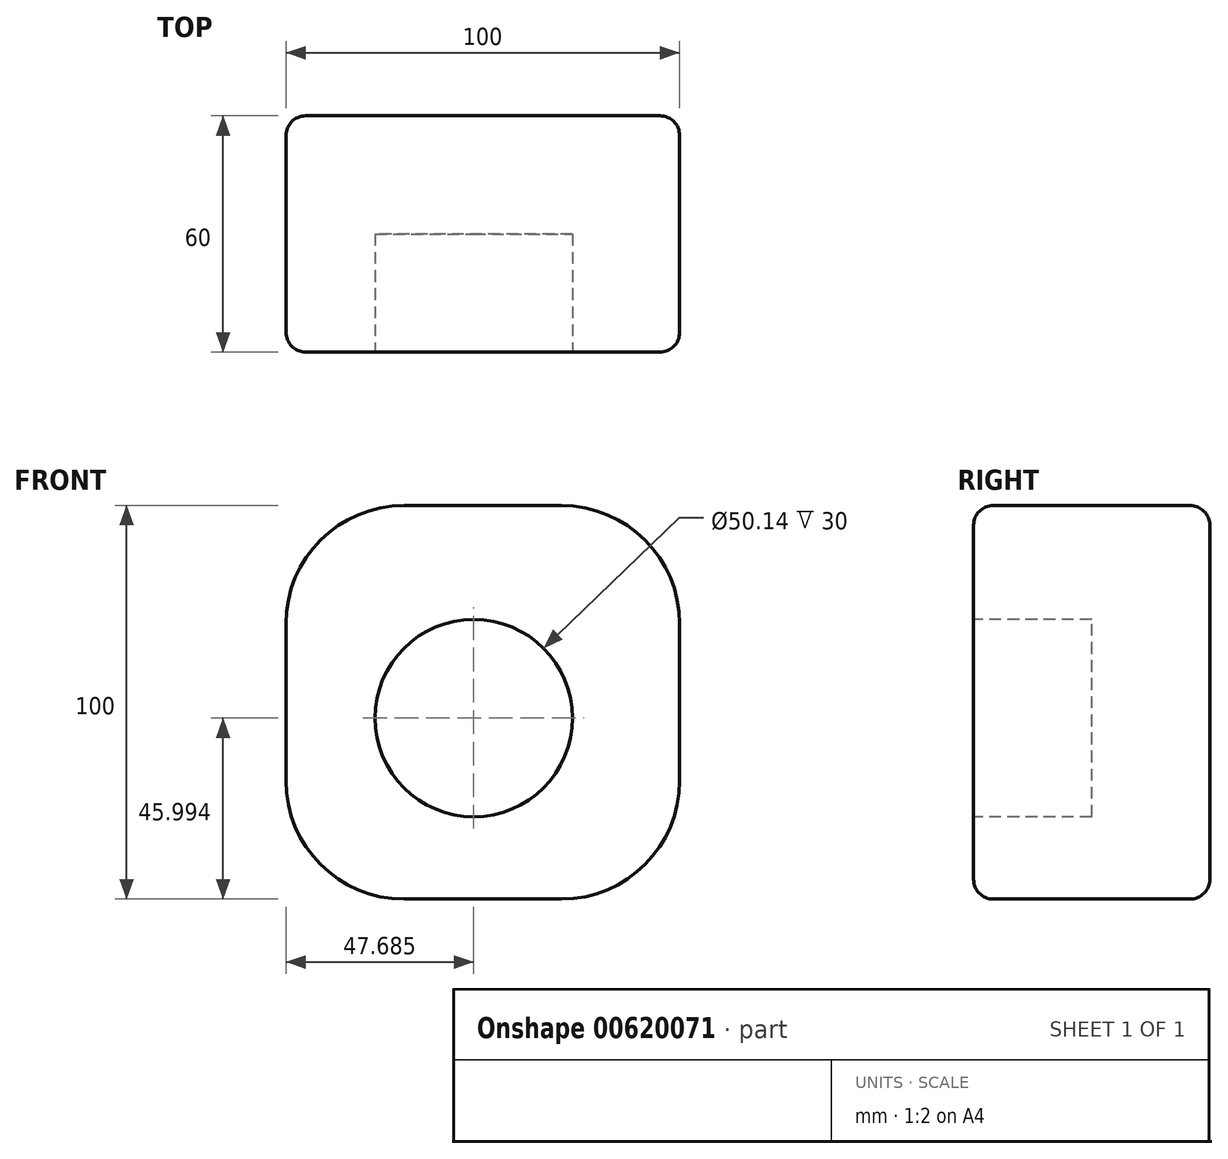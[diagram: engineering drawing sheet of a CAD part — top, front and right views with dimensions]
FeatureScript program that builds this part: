
annotation { "Feature Type Name" : "Feature", "Feature Type Description" : "" }
export const myFeature = defineFeature(function(context is Context, id is Id, definition is map)
    precondition{}
    {
        {
            var Q0;
            Q0=qCreatedBy(makeId("Front.planeOp"),FACE);
            var sketch = newSketch(context, id + "F0", { "sketchPlane" : qUnion([Q0])});
            skLineSegment(sketch, "E0.bottom", {"start": v(-18.67, 72.35) * mm, "end": v(21.33, 72.35) * mm});
            skLineSegment(sketch, "E0.top", {"start": v(-18.67, -27.65) * mm, "end": v(21.33, -27.65) * mm});
            skLineSegment(sketch, "E0.left", {"start": v(-48.67, 42.35) * mm, "end": v(-48.67, 2.35) * mm});
            skLineSegment(sketch, "E0.right", {"start": v(51.33, 42.35) * mm, "end": v(51.33, 2.35) * mm});
            skPoint(sketch, "E1.visualSharp", {"position": v(-48.67, 72.35) * mm});
            skArc(sketch, "E1.filletArc", {"start": v(-18.67, 72.35) * mm, "mid": v(-39.89, 63.56) * mm, "end": v(-48.67, 42.35) * mm});
            skPoint(sketch, "E2.visualSharp", {"position": v(51.33, 72.35) * mm});
            skArc(sketch, "E2.filletArc", {"start": v(51.33, 42.35) * mm, "mid": v(42.54, 63.56) * mm, "end": v(21.33, 72.35) * mm});
            skPoint(sketch, "E3.visualSharp", {"position": v(51.33, -27.65) * mm});
            skArc(sketch, "E3.filletArc", {"start": v(21.33, -27.65) * mm, "mid": v(42.54, -18.87) * mm, "end": v(51.33, 2.35) * mm});
            skPoint(sketch, "E4.visualSharp", {"position": v(-48.67, -27.65) * mm});
            skArc(sketch, "E4.filletArc", {"start": v(-48.67, 2.35) * mm, "mid": v(-39.89, -18.87) * mm, "end": v(-18.67, -27.65) * mm});
            skSolve(sketch);
        }
        {
            var Q0;
            Q0 = qSketchRegion(id + "FFw2fI9CnhElgfZ_0", true);
            var Q1;
            Q1 = qSketchRegion(id + "F0", true);
            extrude(context, id + "F1", {"entities" : qUnion([Q0, Q1]), "depth" : 60 * mm, "offsetDistance" : 25 * mm});
        }
        {
            var Q0;
            Q0=makeQuery(id+"F1.opExtrude","SWEPT_FACE",FACE,{"disambiguationData":[OSD([sQuery(id+"F0.wireOp",EDGE,"E2.filletArc")])]});
            fillet(context, id + "F2", {"entities" : qUnion([Q0]), "radius" : 5 * mm, "tangentPropagation" : true, "allowEdgeOverflow" : false});
        }
        {
            var Q0;
            Q0=makeQuery(id+"F1.opExtrude","CAP_FACE",FACE,{"disambiguationData":[OSD([sQuery(id+"F0.wireOp",EDGE,"E0.bottom"),sQuery(id+"F0.wireOp",EDGE,"E0.top"),sQuery(id+"F0.wireOp",EDGE,"E0.left"),sQuery(id+"F0.wireOp",EDGE,"E0.right"),sQuery(id+"F0.wireOp",EDGE,"E1.filletArc"),sQuery(id+"F0.wireOp",EDGE,"E2.filletArc"),sQuery(id+"F0.wireOp",EDGE,"E3.filletArc"),sQuery(id+"F0.wireOp",EDGE,"E4.filletArc")])],"isStart":false});
            var sketch = newSketch(context, id + "F3", { "sketchPlane" : qUnion([Q0])});
            skCircle(sketch, "E5", {"center": v(-0.98, 18.34) * mm, "radius": 25.07 * mm});
            skSolve(sketch);
        }
        {
            var Q0;
            Q0=makeQuery(id+"F3.imprint","IMPRINT",FACE,{"disambiguationData":[TD([[makeQuery(id+"F3.imprint","IMPRINT",EDGE,{"derivedFrom":sQuery(id+"F3.wireOp",EDGE,"E5")}),1.0]])]});
            extrude(context, id + "F4", {"entities" : qUnion([Q0]), "operationType" : NewBodyOperationType.REMOVE, "oppositeDirection" : true, "depth" : 30 * mm, "offsetDistance" : 25 * mm});
        }
    });
